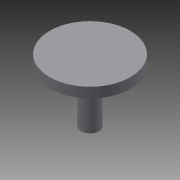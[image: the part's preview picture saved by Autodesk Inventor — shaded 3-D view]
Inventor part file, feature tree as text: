
AUTODESK INVENTOR PART (.ipt)
format: ipt  version: 2015 (Build 190159000, 159)  size: 83,456 bytes
history: native  units: in
note: dims shown in document units (in); Inventor stores cm internally (conversion verified against a paired STEP export)
features: revolve x1, sketch x1
ambient origin geometry x8: Origin, YZ Plane, XZ Plane, XY Plane, X Axis, Y Axis, Z Axis, Center Point
bodies: Solid1 (feature_tree)
feature tree (2):
  revolve  "Revolution1"  [1 undecoded]
  sketch  "Sketch1"  dims[d0=0.25in d2=0.3in d3=1.0in d4=1.0in d5=0.225in d6=0.35in d7=90.0deg]
note: 1 required parameter value undecoded (feature->parameter linkage not recoverable at this tier; creation-order binding heuristic only, values carry confidence <= 0.55)
